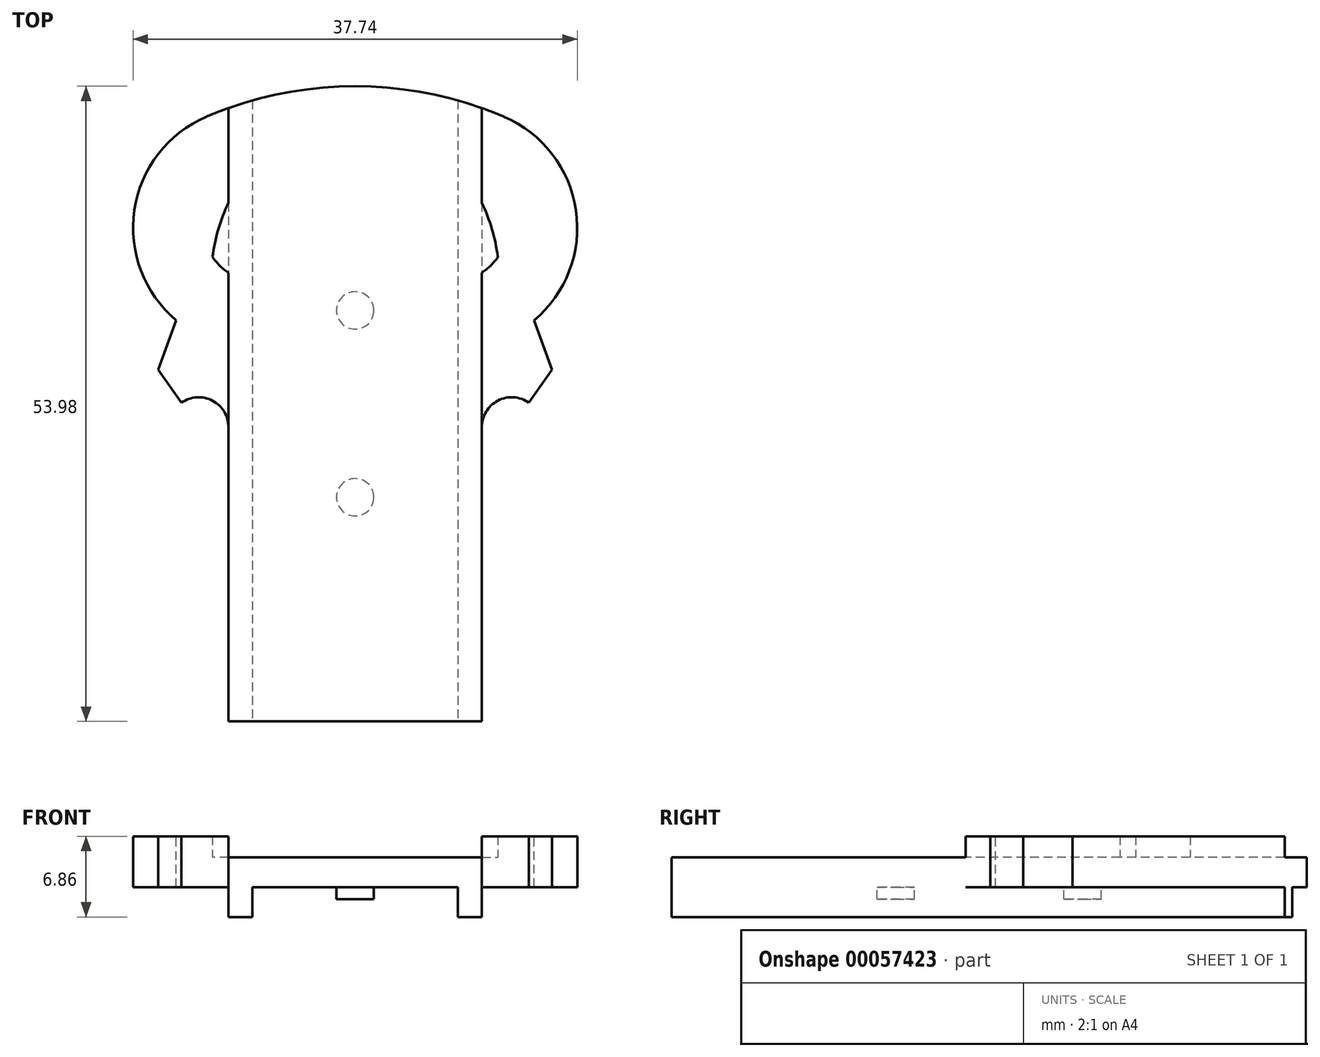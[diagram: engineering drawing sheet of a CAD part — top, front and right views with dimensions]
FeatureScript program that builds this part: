
annotation { "Feature Type Name" : "Feature", "Feature Type Description" : "" }
export const myFeature = defineFeature(function(context is Context, id is Id, definition is map)
    precondition{}
    {
        {
            var Q0;
            Q0=qCreatedBy(makeId("Top.planeOp"),FACE);
            var sketch = newSketch(context, id + "F0", { "sketchPlane" : qUnion([Q0])});
            skCircle(sketch, "E0", {"center": v(0, 0) * mm, "radius": 1.59 * mm});
            skCircle(sketch, "E1", {"center": v(0, 7.94) * mm, "radius": 1.59 * mm});
            skCircle(sketch, "E2", {"center": v(0, -7.94) * mm, "radius": 1.59 * mm});
            skLineSegment(sketch, "E3.bottom", {"start": v(-8.73, 26.99) * mm, "end": v(8.73, 26.99) * mm});
            skLineSegment(sketch, "E3.top", {"start": v(-8.73, -26.99) * mm, "end": v(8.73, -26.99) * mm});
            skLineSegment(sketch, "E3.left", {"start": v(-8.73, 26.99) * mm, "end": v(-8.73, -26.99) * mm});
            skLineSegment(sketch, "E3.right", {"start": v(8.73, 26.99) * mm, "end": v(8.73, -26.99) * mm});
            skLineSegment(sketch, "E4", {"start": v(-8.73, 0) * mm, "end": v(8.73, 0) * mm});
            skLineSegment(sketch, "E5.bottom", {"start": v(-8.73, 26.99) * mm, "end": v(-10.76, 26.99) * mm});
            skLineSegment(sketch, "E5.top", {"start": v(-8.73, -26.99) * mm, "end": v(-10.76, -26.99) * mm});
            skLineSegment(sketch, "E5.right", {"start": v(-10.76, 26.99) * mm, "end": v(-10.76, -26.99) * mm});
            skLineSegment(sketch, "E6.bottom", {"start": v(8.73, 26.99) * mm, "end": v(10.76, 26.99) * mm});
            skLineSegment(sketch, "E6.top", {"start": v(8.73, -26.99) * mm, "end": v(10.76, -26.99) * mm});
            skLineSegment(sketch, "E6.right", {"start": v(10.76, 26.99) * mm, "end": v(10.76, -26.99) * mm});
            skSolve(sketch);
        }
        {
            var Q0;
            Q0=makeQuery(id+"F0.imprint","IMPRINT",FACE,{"disambiguationData":[TD([[makeQuery(id+"F0.imprint","IMPRINT",EDGE,{"derivedFrom":sQuery(id+"F0.wireOp",EDGE,"E1")}),-1.0]])]});
            var Q1;
            Q1=makeQuery(id+"F0.imprint","IMPRINT",FACE,{"disambiguationData":[TD([[makeQuery(id+"F0.imprint","IMPRINT",EDGE,{"derivedFrom":sQuery(id+"F0.wireOp",EDGE,"E1")}),1.0]])]});
            var Q2;
            Q2=makeQuery(id+"F0.imprint","IMPRINT",FACE,{"disambiguationData":[TD([[makeQuery(id+"F0.imprint","IMPRINT",EDGE,{"derivedFrom":sQuery(id+"F0.wireOp",EDGE,"E2")}),-1.0]])]});
            var Q3;
            Q3=makeQuery(id+"F0.imprint","IMPRINT",FACE,{"disambiguationData":[TD([[makeQuery(id+"F0.imprint","IMPRINT",EDGE,{"derivedFrom":sQuery(id+"F0.wireOp",EDGE,"E2")}),1.0]])]});
            var Q4;
            {var subQ0=sQuery(id+"F0.wireOp",EDGE,"E4");var subQ1=sQuery(id+"F0.wireOp",EDGE,"E0");var subQ2=makeQuery(id+"F0.imprint","INTERSECT",VERTEX,{"disambiguationData":[OD(0.0)],"derivedFrom":[subQ1,subQ0]});Q4=makeQuery(id+"F0.imprint","IMPRINT",FACE,{"disambiguationData":[TD([[makeQuery(id+"F0.imprint","IMPRINT",EDGE,{"disambiguationData":[TD([[subQ2,1.0]])],"derivedFrom":subQ1}),1.0]])]});}
            var Q5;
            {var subQ3=sQuery(id+"F0.wireOp",EDGE,"E6.bottom");Q5=makeQuery(id+"F0.imprint","IMPRINT",FACE,{"disambiguationData":[TD([[makeQuery(id+"F0.imprint","IMPRINT",EDGE,{"derivedFrom":subQ3}),-1.0]])]});}
            var Q6;
            {var subQ3=sQuery(id+"F0.wireOp",EDGE,"E5.bottom");Q6=makeQuery(id+"F0.imprint","IMPRINT",FACE,{"disambiguationData":[TD([[makeQuery(id+"F0.imprint","IMPRINT",EDGE,{"derivedFrom":subQ3}),1.0]])]});}
            var Q7;
            {var subQ0=sQuery(id+"F0.wireOp",EDGE,"E4");var subQ1=sQuery(id+"F0.wireOp",EDGE,"E0");var subQ2=makeQuery(id+"F0.imprint","INTERSECT",VERTEX,{"disambiguationData":[OD(0.0)],"derivedFrom":[subQ1,subQ0]});Q7=makeQuery(id+"F0.imprint","IMPRINT",FACE,{"disambiguationData":[TD([[makeQuery(id+"F0.imprint","IMPRINT",EDGE,{"disambiguationData":[TD([[subQ2,-1.0]])],"derivedFrom":subQ1}),1.0]])]});}
            extrude(context, id + "F1", {"entities" : qUnion([Q0, Q1, Q2, Q3, Q4, Q5, Q6, Q7]), "depth" : 2.54 * mm});
        }
        {
            var Q0;
            {var subQ3=sQuery(id+"F0.wireOp",EDGE,"E6.bottom");Q0=makeQuery(id+"F0.imprint","IMPRINT",FACE,{"disambiguationData":[TD([[makeQuery(id+"F0.imprint","IMPRINT",EDGE,{"derivedFrom":subQ3}),-1.0]])]});}
            var Q1;
            {var subQ3=sQuery(id+"F0.wireOp",EDGE,"E5.bottom");Q1=makeQuery(id+"F0.imprint","IMPRINT",FACE,{"disambiguationData":[TD([[makeQuery(id+"F0.imprint","IMPRINT",EDGE,{"derivedFrom":subQ3}),1.0]])]});}
            extrude(context, id + "F2", {"entities" : qUnion([Q0, Q1]), "operationType" : NewBodyOperationType.ADD, "oppositeDirection" : true, "depth" : 2.54 * mm});
        }
        {
            var Q0;
            Q0=makeQuery(id+"F0.imprint","IMPRINT",FACE,{"disambiguationData":[TD([[makeQuery(id+"F0.imprint","IMPRINT",EDGE,{"derivedFrom":sQuery(id+"F0.wireOp",EDGE,"E1")}),1.0]])]});
            var Q1;
            Q1=makeQuery(id+"F0.imprint","IMPRINT",FACE,{"disambiguationData":[TD([[makeQuery(id+"F0.imprint","IMPRINT",EDGE,{"derivedFrom":sQuery(id+"F0.wireOp",EDGE,"E2")}),1.0]])]});
            extrude(context, id + "F3", {"entities" : qUnion([Q0, Q1]), "operationType" : NewBodyOperationType.ADD, "oppositeDirection" : true, "depth" : 1.02 * mm});
        }
        {
            var Q0;
            Q0=makeQuery(id+"F1.opExtrude","CAP_FACE",FACE,{"disambiguationData":[OSD([sQuery(id+"F0.wireOp",EDGE,"E3.bottom"),sQuery(id+"F0.wireOp",EDGE,"E3.top"),sQuery(id+"F0.wireOp",EDGE,"E5.bottom"),sQuery(id+"F0.wireOp",EDGE,"E5.top"),sQuery(id+"F0.wireOp",EDGE,"E5.right"),sQuery(id+"F0.wireOp",EDGE,"E6.bottom"),sQuery(id+"F0.wireOp",EDGE,"E6.top"),sQuery(id+"F0.wireOp",EDGE,"E6.right")])],"isStart":false});
            var sketch = newSketch(context, id + "F4", { "sketchPlane" : qUnion([Q0])});
            skLineSegment(sketch, "E7.0.0", {"start": v(10.76, 26.99) * mm, "end": v(-10.76, 26.99) * mm});
            skLineSegment(sketch, "E7.0.1", {"start": v(-10.76, 26.99) * mm, "end": v(-10.76, -26.99) * mm});
            skLineSegment(sketch, "E7.0.2", {"start": v(-10.76, -26.99) * mm, "end": v(10.76, -26.99) * mm});
            skLineSegment(sketch, "E7.0.3", {"start": v(10.76, -26.99) * mm, "end": v(10.76, 26.99) * mm});
            skLineSegment(sketch, "E8.bottom", {"start": v(-10.76, -26.99) * mm, "end": v(-6.52, -26.99) * mm});
            skLineSegment(sketch, "E8.top", {"start": v(-10.76, -1.98) * mm, "end": v(-6.52, -1.98) * mm, "construction": true});
            skLineSegment(sketch, "E8.left", {"start": v(-10.76, -26.99) * mm, "end": v(-10.76, -1.98) * mm});
            skLineSegment(sketch, "E8.right", {"start": v(-6.52, -26.99) * mm, "end": v(-6.52, -1.98) * mm});
            skLineSegment(sketch, "E9.bottom", {"start": v(-6.52, -1.98) * mm, "end": v(-5, -1.98) * mm});
            skLineSegment(sketch, "E9.top", {"start": v(-6.52, -26.99) * mm, "end": v(-5, -26.99) * mm});
            skLineSegment(sketch, "E9.left", {"start": v(-6.52, -1.98) * mm, "end": v(-6.52, -26.99) * mm});
            skLineSegment(sketch, "E9.right", {"start": v(-5, -1.98) * mm, "end": v(-5, -26.99) * mm});
            skLineSegment(sketch, "E10.bottom", {"start": v(-5, -1.98) * mm, "end": v(-0.76, -1.98) * mm, "construction": true});
            skLineSegment(sketch, "E10.top", {"start": v(-5, -26.99) * mm, "end": v(-0.76, -26.99) * mm});
            skLineSegment(sketch, "E10.right", {"start": v(-0.76, -1.98) * mm, "end": v(-0.76, -26.99) * mm});
            skLineSegment(sketch, "E11.bottom", {"start": v(-0.76, -1.98) * mm, "end": v(0.76, -1.98) * mm});
            skLineSegment(sketch, "E11.top", {"start": v(-0.76, -26.99) * mm, "end": v(0.76, -26.99) * mm});
            skLineSegment(sketch, "E11.right", {"start": v(0.76, -1.98) * mm, "end": v(0.76, -26.99) * mm});
            skLineSegment(sketch, "E12.bottom", {"start": v(0.76, -1.98) * mm, "end": v(5, -1.98) * mm, "construction": true});
            skLineSegment(sketch, "E12.top", {"start": v(0.76, -26.99) * mm, "end": v(5, -26.99) * mm});
            skLineSegment(sketch, "E12.right", {"start": v(5, -1.98) * mm, "end": v(5, -26.99) * mm});
            skLineSegment(sketch, "E13.bottom", {"start": v(5, -1.98) * mm, "end": v(6.52, -1.98) * mm});
            skLineSegment(sketch, "E13.top", {"start": v(5, -26.99) * mm, "end": v(6.52, -26.99) * mm});
            skLineSegment(sketch, "E13.right", {"start": v(6.52, -1.98) * mm, "end": v(6.52, -26.99) * mm});
            skLineSegment(sketch, "E14.bottom", {"start": v(6.52, -1.98) * mm, "end": v(10.76, -1.98) * mm, "construction": true});
            skLineSegment(sketch, "E14.top", {"start": v(6.52, -26.99) * mm, "end": v(10.76, -26.99) * mm});
            skLineSegment(sketch, "E14.right", {"start": v(10.76, -1.98) * mm, "end": v(10.76, -26.99) * mm});
            skLineSegment(sketch, "E15", {"start": v(-12.65, 24.4) * mm, "end": v(-10.76, 24.4) * mm, "construction": true});
            skLineSegment(sketch, "E16", {"start": v(12.65, 24.4) * mm, "end": v(10.76, 24.4) * mm, "construction": true});
            skArc(sketch, "E17", {"start": v(-10.76, -1.98) * mm, "mid": v(-12.13, 0.27) * mm, "end": v(-14.76, 0.1) * mm});
            skArc(sketch, "E18", {"start": v(14.76, 0.1) * mm, "mid": v(12.13, 0.27) * mm, "end": v(10.76, -1.98) * mm});
            skLineSegment(sketch, "E19", {"start": v(14.76, 0.1) * mm, "end": v(16.73, 2.9) * mm});
            skLineSegment(sketch, "E20", {"start": v(-14.76, 0.1) * mm, "end": v(-16.73, 2.9) * mm});
            skLineSegment(sketch, "E21", {"start": v(-16.73, 2.9) * mm, "end": v(-15.2, 7.1) * mm});
            skLineSegment(sketch, "E22", {"start": v(16.73, 2.9) * mm, "end": v(15.2, 7.1) * mm});
            skArc(sketch, "E23", {"start": v(12.65, 24.4) * mm, "mid": v(0, 26.99) * mm, "end": v(-12.65, 24.4) * mm});
            skArc(sketch, "E24", {"start": v(15.2, 7.1) * mm, "mid": v(18.76, 16.46) * mm, "end": v(12.65, 24.4) * mm});
            skArc(sketch, "E25", {"start": v(-12.65, 24.4) * mm, "mid": v(-18.76, 16.46) * mm, "end": v(-15.2, 7.1) * mm});
            skLineSegment(sketch, "E26", {"start": v(-1.27, 7.42) * mm, "end": v(-1.27, 3.1) * mm});
            skLineSegment(sketch, "E27", {"start": v(1.27, 7.42) * mm, "end": v(1.27, 3.1) * mm});
            skArc(sketch, "E28", {"start": v(-1.27, 7.42) * mm, "mid": v(-2.58, 6.14) * mm, "end": v(-3.05, 4.37) * mm});
            skArc(sketch, "E29", {"start": v(-3.05, 4.37) * mm, "mid": v(-2.48, 3.28) * mm, "end": v(-1.27, 3.1) * mm});
            skArc(sketch, "E30", {"start": v(3.05, 4.37) * mm, "mid": v(2.58, 6.14) * mm, "end": v(1.27, 7.42) * mm});
            skArc(sketch, "E31", {"start": v(1.27, 3.1) * mm, "mid": v(2.48, 3.28) * mm, "end": v(3.05, 4.37) * mm});
            skArc(sketch, "E32", {"start": v(-12.12, 12.48) * mm, "mid": v(-8.34, 10.29) * mm, "end": v(-4.25, 11.84) * mm});
            skArc(sketch, "E33", {"start": v(4.25, 11.84) * mm, "mid": v(8.34, 10.29) * mm, "end": v(12.12, 12.48) * mm});
            skArc(sketch, "E34", {"start": v(-9.88, 18.7) * mm, "mid": v(-11.34, 15.71) * mm, "end": v(-12.12, 12.48) * mm});
            skArc(sketch, "E35", {"start": v(12.12, 12.48) * mm, "mid": v(11.34, 15.71) * mm, "end": v(9.88, 18.7) * mm});
            skArc(sketch, "E36", {"start": v(-9.88, 18.7) * mm, "mid": v(-8.56, 14.05) * mm, "end": v(-4.25, 11.84) * mm});
            skArc(sketch, "E37", {"start": v(4.25, 11.84) * mm, "mid": v(8.56, 14.05) * mm, "end": v(9.88, 18.7) * mm});
            skLineSegment(sketch, "E38", {"start": v(-12.12, 12.48) * mm, "end": v(-10.76, 12.48) * mm, "construction": true});
            skLineSegment(sketch, "E39", {"start": v(12.12, 12.48) * mm, "end": v(10.76, 12.48) * mm, "construction": true});
            skSolve(sketch);
        }
        {
            var Q0;
            {var subQ0=sQuery(id+"F4.wireOp",EDGE,"E7.0.1");var subQ1=sQuery(id+"F4.wireOp",EDGE,"E7.0.0");var subQ2=makeQuery(id+"F4.imprint","INTERSECT",VERTEX,{"derivedFrom":[subQ1,subQ0]});Q0=makeQuery(id+"F4.imprint","IMPRINT",FACE,{"disambiguationData":[TD([[makeQuery(id+"F4.imprint","IMPRINT",EDGE,{"disambiguationData":[TD([[subQ2,-1.0]])],"derivedFrom":subQ1}),-1.0]])]});}
            var Q1;
            {var subQ0=sQuery(id+"F4.wireOp",EDGE,"E7.0.3");var subQ1=sQuery(id+"F4.wireOp",EDGE,"E7.0.0");var subQ2=makeQuery(id+"F4.imprint","INTERSECT",VERTEX,{"derivedFrom":[subQ1,subQ0]});Q1=makeQuery(id+"F4.imprint","IMPRINT",FACE,{"disambiguationData":[TD([[makeQuery(id+"F4.imprint","IMPRINT",EDGE,{"disambiguationData":[TD([[subQ2,1.0]])],"derivedFrom":subQ1}),-1.0]])]});}
            var Q2;
            {var subQ4=sQuery(id+"F4.wireOp",EDGE,"E17");Q2=makeQuery(id+"F4.imprint","IMPRINT",FACE,{"disambiguationData":[TD([[makeQuery(id+"F4.imprint","IMPRINT",EDGE,{"derivedFrom":subQ4}),-1.0]])]});}
            var Q3;
            {var subQ0=sQuery(id+"F4.wireOp",EDGE,"E18");Q3=makeQuery(id+"F4.imprint","IMPRINT",FACE,{"disambiguationData":[TD([[makeQuery(id+"F4.imprint","IMPRINT",EDGE,{"derivedFrom":subQ0}),-1.0]])]});}
            var Q4;
            {var subQ5=sQuery(id+"F4.wireOp",EDGE,"E37");Q4=makeQuery(id+"F4.imprint","IMPRINT",FACE,{"disambiguationData":[TD([[makeQuery(id+"F4.imprint","IMPRINT",EDGE,{"derivedFrom":subQ5}),-1.0]])]});}
            var Q5;
            Q5=makeQuery(id+"F4.imprint","IMPRINT",FACE,{"disambiguationData":[TD([[makeQuery(id+"F4.imprint","IMPRINT",EDGE,{"derivedFrom":sQuery(id+"F4.wireOp",EDGE,"E13.bottom")}),-1.0]])]});
            var Q6;
            Q6=makeQuery(id+"F4.imprint","IMPRINT",FACE,{"disambiguationData":[TD([[makeQuery(id+"F4.imprint","IMPRINT",EDGE,{"derivedFrom":sQuery(id+"F4.wireOp",EDGE,"E9.bottom")}),-1.0]])]});
            var Q7;
            {var subQ5=sQuery(id+"F4.wireOp",EDGE,"E36");Q7=makeQuery(id+"F4.imprint","IMPRINT",FACE,{"disambiguationData":[TD([[makeQuery(id+"F4.imprint","IMPRINT",EDGE,{"derivedFrom":subQ5}),-1.0]])]});}
            var Q8;
            Q8=makeQuery(id+"F4.imprint","IMPRINT",FACE,{"disambiguationData":[TD([[makeQuery(id+"F4.imprint","IMPRINT",EDGE,{"derivedFrom":sQuery(id+"F4.wireOp",EDGE,"E27")}),1.0]])]});
            var Q9;
            Q9=makeQuery(id+"F4.imprint","IMPRINT",FACE,{"disambiguationData":[TD([[makeQuery(id+"F4.imprint","IMPRINT",EDGE,{"derivedFrom":sQuery(id+"F4.wireOp",EDGE,"E26")}),-1.0]])]});
            var Q10;
            Q10=makeQuery(id+"F4.imprint","IMPRINT",FACE,{"disambiguationData":[TD([[makeQuery(id+"F4.imprint","IMPRINT",EDGE,{"derivedFrom":sQuery(id+"F4.wireOp",EDGE,"E8.bottom")}),1.0]])]});
            var Q11;
            Q11=makeQuery(id+"F4.imprint","IMPRINT",FACE,{"disambiguationData":[TD([[makeQuery(id+"F4.imprint","IMPRINT",EDGE,{"derivedFrom":sQuery(id+"F4.wireOp",EDGE,"E11.bottom")}),-1.0]])]});
            var Q12;
            {var subQ0=sQuery(id+"F4.wireOp",EDGE,"E35");var subQ1=sQuery(id+"F4.wireOp",EDGE,"E7.0.3");var subQ2=makeQuery(id+"F4.imprint","INTERSECT",VERTEX,{"derivedFrom":[subQ1,subQ0]});Q12=makeQuery(id+"F4.imprint","IMPRINT",FACE,{"disambiguationData":[TD([[makeQuery(id+"F4.imprint","IMPRINT",EDGE,{"disambiguationData":[TD([[subQ2,-1.0]])],"derivedFrom":subQ1}),1.0]])]});}
            var Q13;
            {var subQ0=sQuery(id+"F4.wireOp",EDGE,"E34");var subQ1=sQuery(id+"F4.wireOp",EDGE,"E7.0.1");var subQ2=makeQuery(id+"F4.imprint","INTERSECT",VERTEX,{"derivedFrom":[subQ1,subQ0]});Q13=makeQuery(id+"F4.imprint","IMPRINT",FACE,{"disambiguationData":[TD([[makeQuery(id+"F4.imprint","IMPRINT",EDGE,{"disambiguationData":[TD([[subQ2,-1.0]])],"derivedFrom":subQ1}),-1.0]])]});}
            var Q14;
            Q14=makeQuery(id+"F1.opExtrude","CAP_FACE",FACE,{"disambiguationData":[OSD([sQuery(id+"F0.wireOp",EDGE,"E3.bottom"),sQuery(id+"F0.wireOp",EDGE,"E3.top"),sQuery(id+"F0.wireOp",EDGE,"E5.bottom"),sQuery(id+"F0.wireOp",EDGE,"E5.top"),sQuery(id+"F0.wireOp",EDGE,"E5.right"),sQuery(id+"F0.wireOp",EDGE,"E6.bottom"),sQuery(id+"F0.wireOp",EDGE,"E6.top"),sQuery(id+"F0.wireOp",EDGE,"E6.right")])],"isStart":true});
            extrude(context, id + "F5", {"entities" : qUnion([Q0, Q1, Q2, Q3, Q4, Q5, Q6, Q7, Q8, Q9, Q10, Q11, Q12, Q13]), "operationType" : NewBodyOperationType.ADD, "endBound" : BoundingType.UP_TO_SURFACE, "oppositeDirection" : true, "endBoundEntityFace" : qUnion([Q14]), "depth" : 25.4 * mm});
        }
        {
            var Q0;
            {var subQ0=sQuery(id+"F4.wireOp",EDGE,"E7.0.1");var subQ1=sQuery(id+"F4.wireOp",EDGE,"E7.0.0");var subQ2=makeQuery(id+"F4.imprint","INTERSECT",VERTEX,{"derivedFrom":[subQ1,subQ0]});Q0=makeQuery(id+"F4.imprint","IMPRINT",FACE,{"disambiguationData":[TD([[makeQuery(id+"F4.imprint","IMPRINT",EDGE,{"disambiguationData":[TD([[subQ2,-1.0]])],"derivedFrom":subQ1}),-1.0]])]});}
            var Q1;
            {var subQ0=sQuery(id+"F4.wireOp",EDGE,"E7.0.3");var subQ1=sQuery(id+"F4.wireOp",EDGE,"E7.0.0");var subQ2=makeQuery(id+"F4.imprint","INTERSECT",VERTEX,{"derivedFrom":[subQ1,subQ0]});Q1=makeQuery(id+"F4.imprint","IMPRINT",FACE,{"disambiguationData":[TD([[makeQuery(id+"F4.imprint","IMPRINT",EDGE,{"disambiguationData":[TD([[subQ2,1.0]])],"derivedFrom":subQ1}),-1.0]])]});}
            extrude(context, id + "F6", {"entities" : qUnion([Q0, Q1]), "operationType" : NewBodyOperationType.REMOVE, "oppositeDirection" : true, "depth" : 25.4 * mm});
        }
        {
            var Q0;
            Q0=makeQuery(id+"F4.imprint","IMPRINT",FACE,{"disambiguationData":[TD([[makeQuery(id+"F4.imprint","IMPRINT",EDGE,{"derivedFrom":sQuery(id+"F4.wireOp",EDGE,"E8.bottom")}),1.0]])]});
            var Q1;
            {var subQ4=sQuery(id+"F4.wireOp",EDGE,"E17");Q1=makeQuery(id+"F4.imprint","IMPRINT",FACE,{"disambiguationData":[TD([[makeQuery(id+"F4.imprint","IMPRINT",EDGE,{"derivedFrom":subQ4}),-1.0]])]});}
            var Q2;
            {var subQ0=sQuery(id+"F4.wireOp",EDGE,"E18");Q2=makeQuery(id+"F4.imprint","IMPRINT",FACE,{"disambiguationData":[TD([[makeQuery(id+"F4.imprint","IMPRINT",EDGE,{"derivedFrom":subQ0}),-1.0]])]});}
            extrude(context, id + "F7", {"entities" : qUnion([Q0, Q1, Q2]), "operationType" : NewBodyOperationType.ADD, "depth" : 1.78 * mm});
        }
    });
